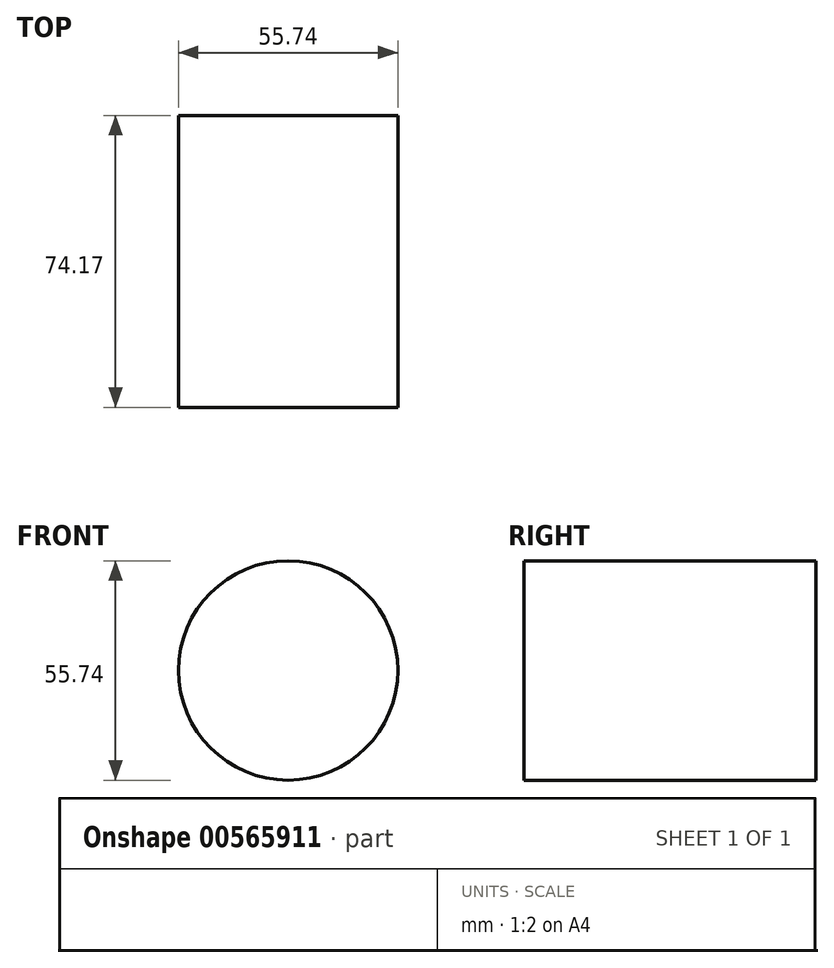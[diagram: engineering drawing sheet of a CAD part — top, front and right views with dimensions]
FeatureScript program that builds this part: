
annotation { "Feature Type Name" : "Feature", "Feature Type Description" : "" }
export const myFeature = defineFeature(function(context is Context, id is Id, definition is map)
    precondition{}
    {
        {
            var Q0;
            Q0=qCreatedBy(makeId("Front.planeOp"),FACE);
            var sketch = newSketch(context, id + "F0", { "sketchPlane" : qUnion([Q0])});
            skCircle(sketch, "E0", {"center": v(0, 0) * mm, "radius": 27.87 * mm});
            skSolve(sketch);
        }
        {
            var Q0;
            Q0=makeQuery(id+"F0.imprint","IMPRINT",FACE,{"disambiguationData":[TD([[makeQuery(id+"F0.imprint","IMPRINT",EDGE,{"derivedFrom":sQuery(id+"F0.wireOp",EDGE,"E0")}),1.0]])]});
            extrude(context, id + "F1", {"entities" : qUnion([Q0]), "depth" : 74.17 * mm, "offsetDistance" : 25.4 * mm});
        }
    });
